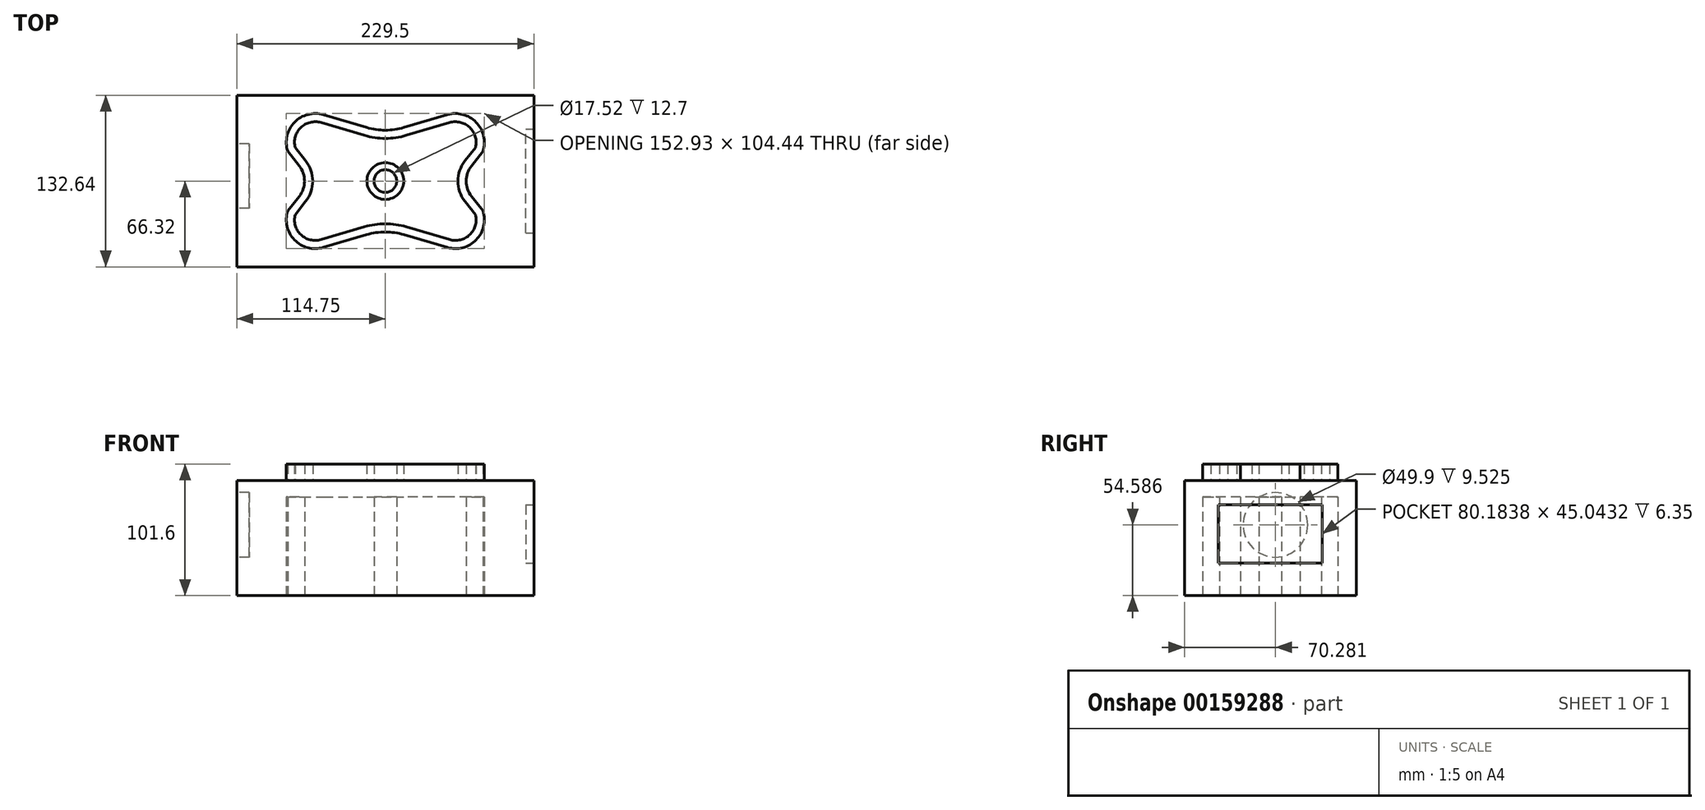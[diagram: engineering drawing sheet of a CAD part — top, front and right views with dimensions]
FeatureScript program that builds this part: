
annotation { "Feature Type Name" : "Feature", "Feature Type Description" : "" }
export const myFeature = defineFeature(function(context is Context, id is Id, definition is map)
    precondition{}
    {
        {
            var Q0;
            Q0=qCreatedBy(makeId("Top.planeOp"),FACE);
            var sketch = newSketch(context, id + "F0", { "sketchPlane" : qUnion([Q0])});
            skLineSegment(sketch, "E0", {"start": v(-66.51, 11.78) * mm, "end": v(-75.4, 23.07) * mm});
            skLineSegment(sketch, "E1", {"start": v(-47.91, 51.32) * mm, "end": v(-14.36, 41.43) * mm});
            skArc(sketch, "E2", {"start": v(-47.91, 51.32) * mm, "mid": v(-70.17, 45.48) * mm, "end": v(-75.4, 23.07) * mm});
            skLineSegment(sketch, "E3.MirrorCS", {"start": v(47.91, 51.32) * mm, "end": v(14.36, 41.43) * mm});
            skArc(sketch, "E4.MirrorCS", {"start": v(47.91, 51.32) * mm, "mid": v(70.17, 45.48) * mm, "end": v(75.4, 23.07) * mm});
            skLineSegment(sketch, "E5.MirrorCS", {"start": v(66.51, 11.78) * mm, "end": v(75.4, 23.07) * mm});
            skLineSegment(sketch, "E6.MirrorCS", {"start": v(66.51, -11.78) * mm, "end": v(75.4, -23.07) * mm});
            skArc(sketch, "E7.MirrorCS", {"start": v(47.91, -51.32) * mm, "mid": v(70.17, -45.48) * mm, "end": v(75.4, -23.07) * mm});
            skLineSegment(sketch, "E8.MirrorCS", {"start": v(47.91, -51.32) * mm, "end": v(14.36, -41.43) * mm});
            skLineSegment(sketch, "E9.MirrorCS", {"start": v(-66.51, -11.78) * mm, "end": v(-75.4, -23.07) * mm});
            skLineSegment(sketch, "E10.MirrorCS", {"start": v(-47.91, -51.32) * mm, "end": v(-14.36, -41.43) * mm});
            skArc(sketch, "E11.MirrorCS", {"start": v(-47.91, -51.32) * mm, "mid": v(-70.17, -45.48) * mm, "end": v(-75.4, -23.07) * mm});
            skPoint(sketch, "E12.visualSharp", {"position": v(-57.24, 0) * mm});
            skArc(sketch, "E12.filletArc", {"start": v(-66.51, -11.78) * mm, "mid": v(-62.43, 0) * mm, "end": v(-66.51, 11.78) * mm});
            skPoint(sketch, "E13.visualSharp", {"position": v(0, 37.2) * mm});
            skArc(sketch, "E13.filletArc", {"start": v(-14.36, 41.43) * mm, "mid": v(0, 39.35) * mm, "end": v(14.36, 41.43) * mm});
            skPoint(sketch, "E14.visualSharp", {"position": v(0, -37.2) * mm});
            skArc(sketch, "E14.filletArc", {"start": v(14.36, -41.43) * mm, "mid": v(0, -39.35) * mm, "end": v(-14.36, -41.43) * mm});
            skPoint(sketch, "E15.visualSharp", {"position": v(57.24, 0) * mm});
            skArc(sketch, "E15.filletArc", {"start": v(66.51, 11.78) * mm, "mid": v(62.43, 0) * mm, "end": v(66.51, -11.78) * mm});
            skLineSegment(sketch, "E16.bottom", {"start": v(-114.75, 66.32) * mm, "end": v(114.75, 66.32) * mm});
            skLineSegment(sketch, "E16.top", {"start": v(-114.75, -66.32) * mm, "end": v(114.75, -66.32) * mm});
            skLineSegment(sketch, "E16.left", {"start": v(-114.75, 66.32) * mm, "end": v(-114.75, -66.32) * mm});
            skLineSegment(sketch, "E16.right", {"start": v(114.75, 66.32) * mm, "end": v(114.75, -66.32) * mm});
            skPoint(sketch, "E16.middle", {"position": v(0, 0) * mm});
            skArc(sketch, "E17.0", {"start": v(49.7, 45.22) * mm, "mid": v(65.62, 41.06) * mm, "end": v(69.36, 25.03) * mm});
            skLineSegment(sketch, "E17.1", {"start": v(49.7, 45.22) * mm, "end": v(16.16, 35.34) * mm});
            skArc(sketch, "E17.2", {"start": v(-16.16, 35.34) * mm, "mid": v(0, 33) * mm, "end": v(16.16, 35.34) * mm});
            skLineSegment(sketch, "E17.3", {"start": v(-49.7, 45.22) * mm, "end": v(-16.16, 35.34) * mm});
            skArc(sketch, "E18.0", {"start": v(-49.7, 45.22) * mm, "mid": v(-65.25, 41.42) * mm, "end": v(-69.65, 26.03) * mm});
            skLineSegment(sketch, "E18.1", {"start": v(-61.52, 15.7) * mm, "end": v(-69.65, 26.03) * mm});
            skArc(sketch, "E18.2", {"start": v(49.7, -45.22) * mm, "mid": v(65.25, -41.42) * mm, "end": v(69.65, -26.03) * mm});
            skLineSegment(sketch, "E18.3", {"start": v(61.52, -15.7) * mm, "end": v(69.65, -26.03) * mm});
            skArc(sketch, "E18.4", {"start": v(61.52, 15.7) * mm, "mid": v(56.08, 0) * mm, "end": v(61.52, -15.7) * mm});
            skLineSegment(sketch, "E18.5", {"start": v(61.52, 15.7) * mm, "end": v(70.4, 27) * mm});
            skLineSegment(sketch, "E18.6", {"start": v(49.7, -45.22) * mm, "end": v(16.16, -35.34) * mm});
            skArc(sketch, "E18.7", {"start": v(16.16, -35.34) * mm, "mid": v(0, -33) * mm, "end": v(-16.16, -35.34) * mm});
            skLineSegment(sketch, "E18.8", {"start": v(-49.7, -45.22) * mm, "end": v(-16.16, -35.34) * mm});
            skArc(sketch, "E18.9", {"start": v(-49.7, -45.22) * mm, "mid": v(-65.25, -41.42) * mm, "end": v(-69.65, -26.03) * mm});
            skLineSegment(sketch, "E18.10", {"start": v(-61.52, -15.7) * mm, "end": v(-69.65, -26.03) * mm});
            skArc(sketch, "E18.11", {"start": v(-61.52, -15.7) * mm, "mid": v(-56.08, 0) * mm, "end": v(-61.52, 15.7) * mm});
            skCircle(sketch, "E19", {"center": v(0, 0) * mm, "radius": 14.22 * mm});
            skCircle(sketch, "E20", {"center": v(0, 0) * mm, "radius": 8.76 * mm});
            skSolve(sketch);
        }
        {
            var Q0;
            Q0=makeQuery(id+"F0.imprint","IMPRINT",FACE,{"disambiguationData":[TD([[makeQuery(id+"F0.imprint","IMPRINT",EDGE,{"derivedFrom":sQuery(id+"F0.wireOp",EDGE,"E0")}),1.0]])]});
            var Q1;
            Q1=makeQuery(id+"F0.imprint","IMPRINT",FACE,{"disambiguationData":[TD([[makeQuery(id+"F0.imprint","IMPRINT",EDGE,{"derivedFrom":sQuery(id+"F0.wireOp",EDGE,"E20")}),1.0]])]});
            extrude(context, id + "F1", {"entities" : qUnion([Q0, Q1]), "depth" : 12.7 * mm, "hasSecondDirection" : true, "secondDirectionOppositeDirection" : true, "secondDirectionDepth" : 76.2 * mm});
        }
        {
            var Q0;
            {var subQ0=sQuery(id+"F0.wireOp",EDGE,"E17.1");Q0=makeQuery(id+"F0.imprint","IMPRINT",FACE,{"disambiguationData":[TD([[makeQuery(id+"F0.imprint","IMPRINT",EDGE,{"derivedFrom":subQ0}),1.0]])]});}
            extrude(context, id + "F2", {"entities" : qUnion([Q0]), "operationType" : NewBodyOperationType.ADD, "depth" : 12.7 * mm});
        }
        {
            var Q0;
            Q0=makeQuery(id+"F0.imprint","IMPRINT",FACE,{"disambiguationData":[TD([[makeQuery(id+"F0.imprint","IMPRINT",EDGE,{"derivedFrom":sQuery(id+"F0.wireOp",EDGE,"E0")}),-1.0]])]});
            var Q1;
            Q1=makeQuery(id+"F0.imprint","IMPRINT",FACE,{"disambiguationData":[TD([[makeQuery(id+"F0.imprint","IMPRINT",EDGE,{"derivedFrom":sQuery(id+"F0.wireOp",EDGE,"E19")}),1.0]])]});
            extrude(context, id + "F3", {"entities" : qUnion([Q0, Q1]), "operationType" : NewBodyOperationType.ADD, "depth" : 25.4 * mm});
        }
        {
            var Q0;
            {var subQ0=sQuery(id+"F0.wireOp",EDGE,"E17.1");Q0=makeQuery(id+"F0.imprint","IMPRINT",FACE,{"disambiguationData":[TD([[makeQuery(id+"F0.imprint","IMPRINT",EDGE,{"derivedFrom":subQ0}),1.0]])]});}
            extrude(context, id + "F4", {"entities" : qUnion([Q0]), "operationType" : NewBodyOperationType.ADD, "depth" : 12.7 * mm});
        }
        {
            var Q0;
            Q0=makeQuery(id+"F1.opExtrude","SWEPT_FACE",FACE,{"disambiguationData":[OSD([sQuery(id+"F0.wireOp",EDGE,"E16.right")])]});
            var sketch = newSketch(context, id + "F5", { "sketchPlane" : qUnion([Q0])});
            skLineSegment(sketch, "E21.bottom", {"start": v(-40.1, -6.17) * mm, "end": v(40.1, -6.17) * mm});
            skLineSegment(sketch, "E21.top", {"start": v(-40.1, -51.22) * mm, "end": v(40.1, -51.22) * mm});
            skLineSegment(sketch, "E21.left", {"start": v(-40.1, -6.17) * mm, "end": v(-40.1, -51.22) * mm});
            skLineSegment(sketch, "E21.right", {"start": v(40.1, -6.17) * mm, "end": v(40.1, -51.22) * mm});
            skPoint(sketch, "E21.middle", {"position": v(0, -28.7) * mm});
            skSolve(sketch);
        }
        {
            var Q0;
            Q0 = qSketchRegion(id + "F5", true);
            extrude(context, id + "F6", {"entities" : qUnion([Q0]), "operationType" : NewBodyOperationType.REMOVE, "oppositeDirection" : true, "depth" : 6.35 * mm});
        }
        {
            var Q0;
            Q0=makeQuery(id+"F1.opExtrude","SWEPT_FACE",FACE,{"disambiguationData":[OSD([sQuery(id+"F0.wireOp",EDGE,"E16.left")])]});
            var sketch = newSketch(context, id + "F7", { "sketchPlane" : qUnion([Q0])});
            skCircle(sketch, "E22", {"center": v(-3.96, -21.61) * mm, "radius": 24.95 * mm});
            skPoint(sketch, "E22.first.point", {"position": v(18.74, -11.26) * mm});
            skPoint(sketch, "E22.second.point", {"position": v(6, -44.49) * mm});
            skPoint(sketch, "E22.third.point", {"position": v(-16.15, -43.38) * mm});
            skSolve(sketch);
        }
        {
            var Q0;
            Q0=makeQuery(id+"F7.imprint","IMPRINT",FACE,{"disambiguationData":[TD([[makeQuery(id+"F7.imprint","IMPRINT",EDGE,{"derivedFrom":sQuery(id+"F7.wireOp",EDGE,"E22")}),1.0]])]});
            extrude(context, id + "F8", {"entities" : qUnion([Q0]), "operationType" : NewBodyOperationType.REMOVE, "oppositeDirection" : true, "depth" : 9.52 * mm});
        }
    });
